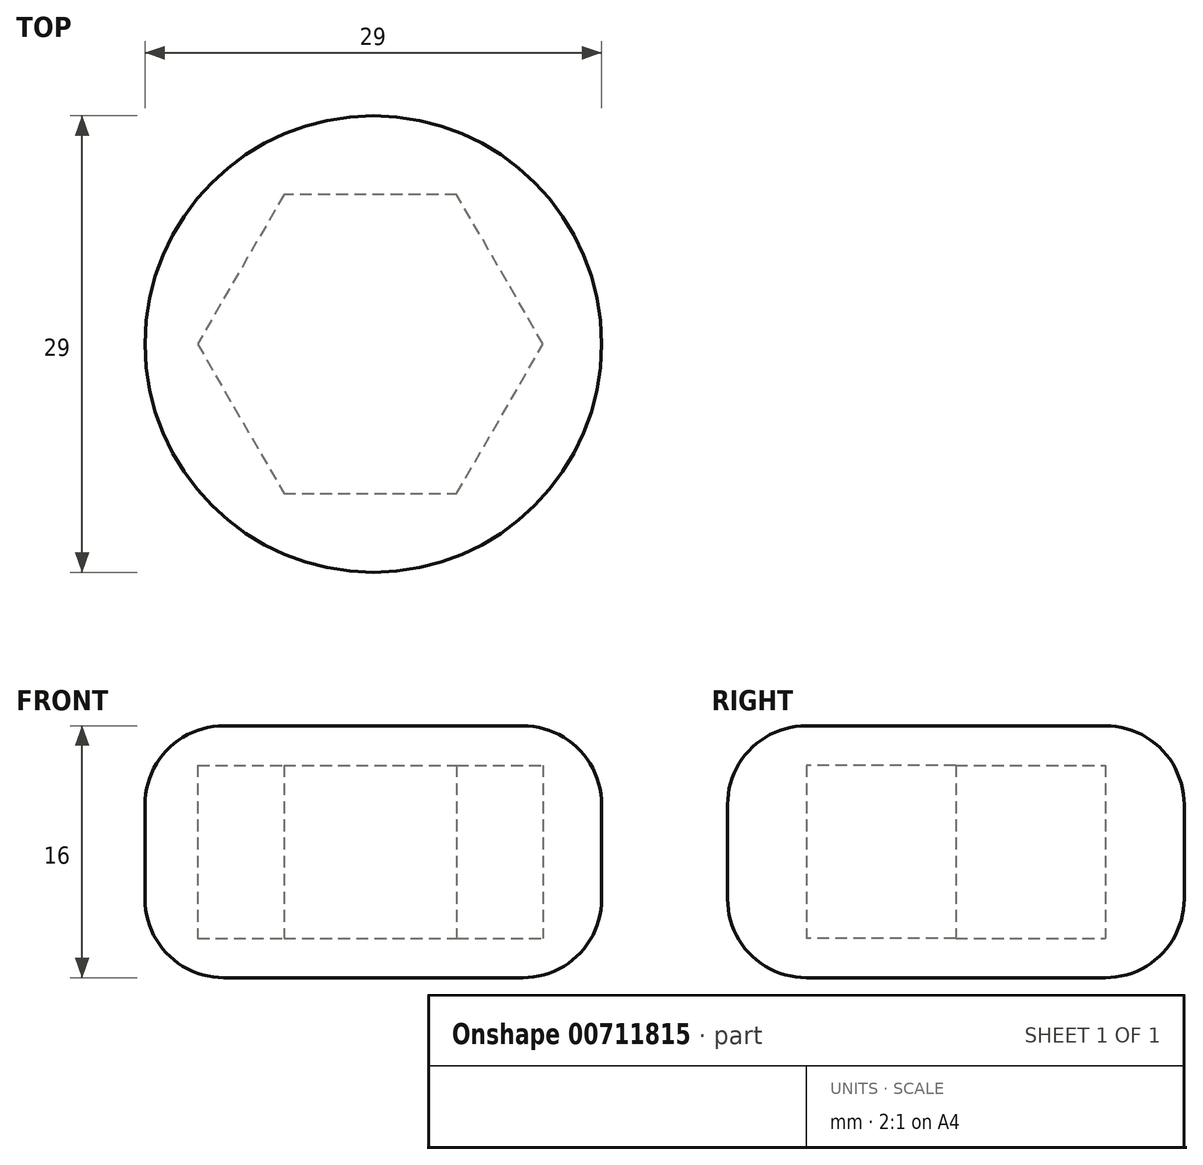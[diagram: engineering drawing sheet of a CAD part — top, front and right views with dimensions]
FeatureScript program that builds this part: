
annotation { "Feature Type Name" : "Feature", "Feature Type Description" : "" }
export const myFeature = defineFeature(function(context is Context, id is Id, definition is map)
    precondition{}
    {
        {
            assignVariable(context, id + "F0", {"name" : "height", "anyValue" : 16 * mm});
        }
        {
            var Q0;
            Q0=qCreatedBy(makeId("Top.planeOp"),FACE);
            var sketch = newSketch(context, id + "F1", { "sketchPlane" : qUnion([Q0])});
            skCircle(sketch, "E0", {"center": v(0, 0) * mm, "radius": 14.5 * mm});
            skSolve(sketch);
        }
        {
            var Q0;
            Q0 = qSketchRegion(id + "F1", true);
            extrude(context, id + "F2", {"entities" : qUnion([Q0]), "endBound" : BoundingType.SYMMETRIC, "depth" : getVariable(context, 'height'), "offsetDistance" : 25 * mm});
        }
        {
            var Q0;
            Q0=qCreatedBy(makeId("Top.planeOp"),FACE);
            var sketch = newSketch(context, id + "F3", { "sketchPlane" : qUnion([Q0])});
            skLineSegment(sketch, "E1", {"start": v(-5.67, -9.5) * mm, "end": v(5.3, -9.5) * mm});
            skLineSegment(sketch, "E2", {"start": v(5.3, -9.5) * mm, "end": v(10.78, 0) * mm});
            skLineSegment(sketch, "E3", {"start": v(10.78, 0) * mm, "end": v(5.3, 9.5) * mm});
            skLineSegment(sketch, "E4", {"start": v(5.3, 9.5) * mm, "end": v(-5.67, 9.5) * mm});
            skLineSegment(sketch, "E5", {"start": v(-5.67, 9.5) * mm, "end": v(-11.16, 0) * mm});
            skLineSegment(sketch, "E6", {"start": v(-11.16, 0) * mm, "end": v(-5.67, -9.5) * mm});
            skLineSegment(sketch, "E7", {"start": v(5.3, 9.5) * mm, "end": v(5.3, -9.5) * mm, "construction": true});
            skLineSegment(sketch, "E8", {"start": v(-5.67, 9.5) * mm, "end": v(10.78, 0) * mm, "construction": true});
            skLineSegment(sketch, "E9", {"start": v(-11.16, 0) * mm, "end": v(5.3, 9.5) * mm, "construction": true});
            skLineSegment(sketch, "E10", {"start": v(0, -9.5) * mm, "end": v(0, 0) * mm, "construction": true});
            skSolve(sketch);
        }
        {
            var Q0;
            Q0=qSketchRegion(id+"F3",true);
            extrude(context, id + "F4", {"entities" : qUnion([Q0]), "operationType" : NewBodyOperationType.REMOVE, "endBound" : BoundingType.SYMMETRIC, "depth" : 11 * mm, "offsetDistance" : 25 * mm});
        }
        {
            var Q0;
            Q0=makeQuery(id+"F2.opExtrude","CAP_EDGE",EDGE,{"disambiguationData":[OSD([sQuery(id+"F1.wireOp",EDGE,"E0")])],"isStart":false});
            var Q1;
            Q1=makeQuery(id+"F2.opExtrude","CAP_EDGE",EDGE,{"disambiguationData":[OSD([sQuery(id+"F1.wireOp",EDGE,"E0")])],"isStart":true});
            fillet(context, id + "F5", {"entities" : qUnion([Q0, Q1]), "radius" : 5 * mm, "tangentPropagation" : true, "allowEdgeOverflow" : false});
        }
    });
